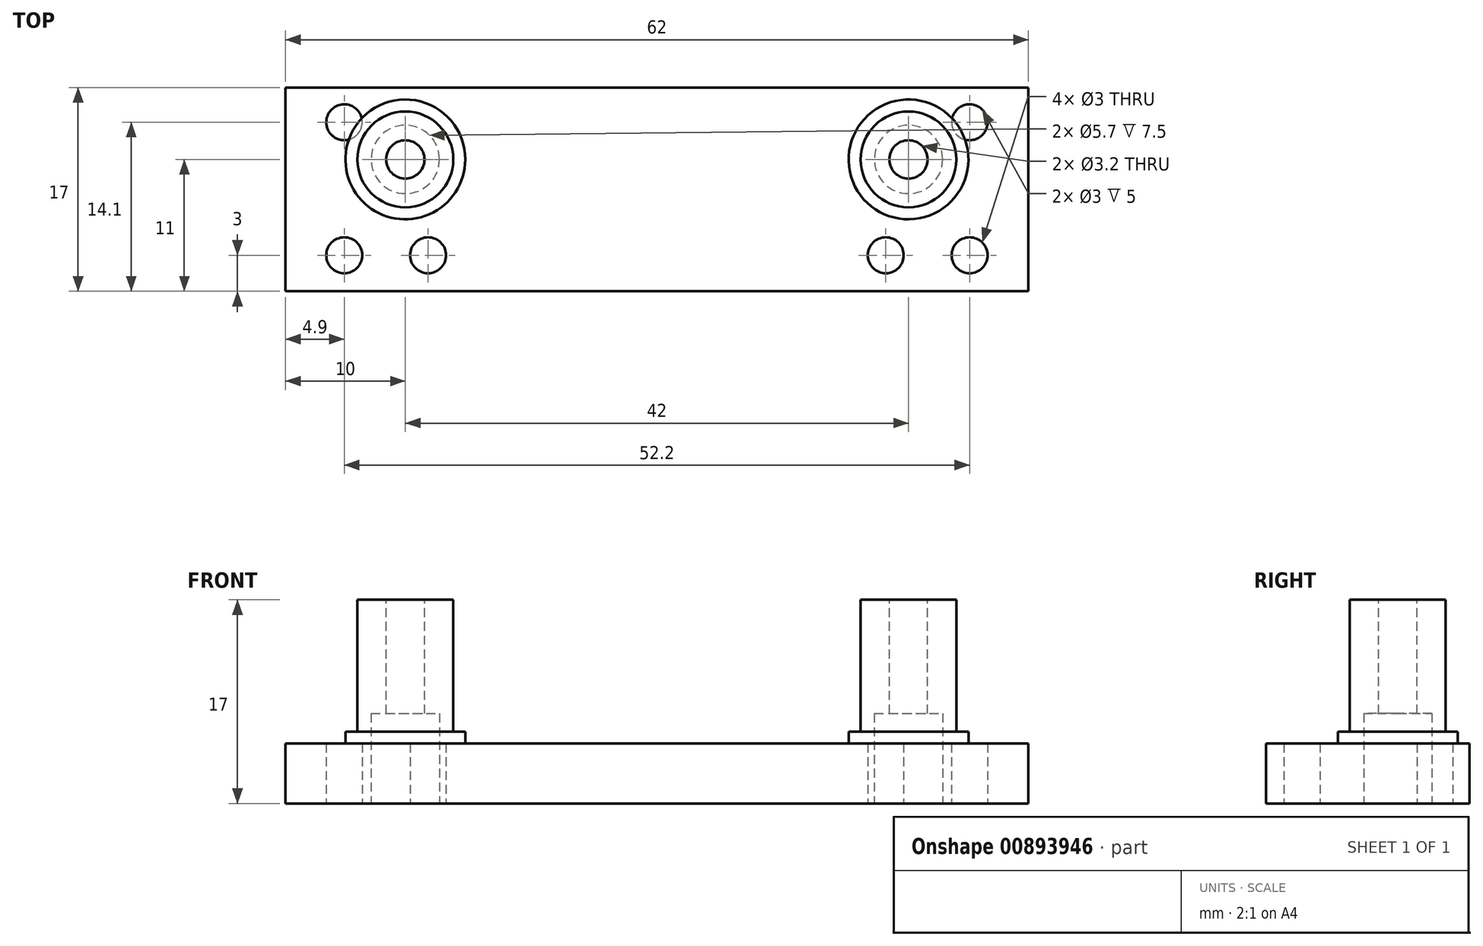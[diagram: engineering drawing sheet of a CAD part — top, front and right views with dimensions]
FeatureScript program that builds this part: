
annotation { "Feature Type Name" : "Feature", "Feature Type Description" : "" }
export const myFeature = defineFeature(function(context is Context, id is Id, definition is map)
    precondition{}
    {
        {
            var Q0;
            Q0=qCreatedBy(makeId("Top.planeOp"),FACE);
            var sketch = newSketch(context, id + "F0", { "sketchPlane" : qUnion([Q0])});
            skLineSegment(sketch, "E0.bottom", {"start": v(0, 0) * mm, "end": v(62, 0) * mm});
            skLineSegment(sketch, "E0.top", {"start": v(0, 17) * mm, "end": v(62, 17) * mm});
            skLineSegment(sketch, "E0.left", {"start": v(0, 0) * mm, "end": v(0, 17) * mm});
            skLineSegment(sketch, "E0.right", {"start": v(62, 0) * mm, "end": v(62, 17) * mm});
            skSolve(sketch);
        }
        {
            var Q0;
            Q0 = qSketchRegion(id + "F0", true);
            extrude(context, id + "F1", {"entities" : qUnion([Q0]), "depth" : 5 * mm, "offsetDistance" : 25 * mm});
        }
        {
            var Q0;
            Q0=makeQuery(id+"F1.opExtrude","CAP_FACE",FACE,{"disambiguationData":[OSD([sQuery(id+"F0.wireOp",EDGE,"E0.bottom"),sQuery(id+"F0.wireOp",EDGE,"E0.top"),sQuery(id+"F0.wireOp",EDGE,"E0.left"),sQuery(id+"F0.wireOp",EDGE,"E0.right")])],"isStart":false});
            var sketch = newSketch(context, id + "F2", { "sketchPlane" : qUnion([Q0])});
            skLineSegment(sketch, "E1", {"start": v(31, 17) * mm, "end": v(31, 0) * mm, "construction": true});
            skLineSegment(sketch, "E2", {"start": v(0, 11) * mm, "end": v(62, 11) * mm, "construction": true});
            skCircle(sketch, "E3", {"center": v(10, 11) * mm, "radius": 5 * mm});
            skCircle(sketch, "E4.MirrorC", {"center": v(52, 11) * mm, "radius": 5 * mm});
            skSolve(sketch);
        }
        {
            var Q0;
            Q0 = qSketchRegion(id + "F2", true);
            extrude(context, id + "F3", {"entities" : qUnion([Q0]), "operationType" : NewBodyOperationType.ADD, "depth" : 1 * mm, "offsetDistance" : 25 * mm});
        }
        {
            var Q0;
            Q0=makeQuery(id+"F3.opExtrude","CAP_FACE",FACE,{"disambiguationData":[OSD([sQuery(id+"F2.wireOp",EDGE,"E4.MirrorC")])],"isStart":false});
            var sketch = newSketch(context, id + "F4", { "sketchPlane" : qUnion([Q0])});
            skCircle(sketch, "E5", {"center": v(52, 11) * mm, "radius": 4 * mm});
            skCircle(sketch, "E6.MirrorC", {"center": v(10, 11) * mm, "radius": 4 * mm});
            skSolve(sketch);
        }
        {
            var Q0;
            Q0 = qSketchRegion(id + "F4", true);
            extrude(context, id + "F5", {"entities" : qUnion([Q0]), "operationType" : NewBodyOperationType.ADD, "depth" : 11 * mm, "offsetDistance" : 25 * mm});
        }
        {
            var Q0;
            Q0=makeQuery(id+"F1.opExtrude","CAP_FACE",FACE,{"disambiguationData":[OSD([sQuery(id+"F0.wireOp",EDGE,"E0.bottom"),sQuery(id+"F0.wireOp",EDGE,"E0.top"),sQuery(id+"F0.wireOp",EDGE,"E0.left"),sQuery(id+"F0.wireOp",EDGE,"E0.right")])],"isStart":true});
            var sketch = newSketch(context, id + "F6", { "sketchPlane" : qUnion([Q0])});
            skCircle(sketch, "E7", {"center": v(52, -11) * mm, "radius": 2.85 * mm});
            skCircle(sketch, "E8.MirrorC", {"center": v(10, -11) * mm, "radius": 2.85 * mm});
            skSolve(sketch);
        }
        {
            var Q0;
            Q0 = qSketchRegion(id + "F6", true);
            extrude(context, id + "F7", {"entities" : qUnion([Q0]), "operationType" : NewBodyOperationType.REMOVE, "oppositeDirection" : true, "depth" : 7.5 * mm, "offsetDistance" : 25 * mm});
        }
        {
            var Q0;
            Q0=makeQuery(id+"F5.opExtrude","CAP_FACE",FACE,{"disambiguationData":[OSD([sQuery(id+"F4.wireOp",EDGE,"E5")])],"isStart":false});
            var sketch = newSketch(context, id + "F8", { "sketchPlane" : qUnion([Q0])});
            skCircle(sketch, "E9", {"center": v(52, 11) * mm, "radius": 1.6 * mm});
            skCircle(sketch, "E10.MirrorC", {"center": v(10, 11) * mm, "radius": 1.6 * mm});
            skSolve(sketch);
        }
        {
            var Q0;
            Q0 = qSketchRegion(id + "F8", true);
            extrude(context, id + "F9", {"entities" : qUnion([Q0]), "operationType" : NewBodyOperationType.REMOVE, "oppositeDirection" : true, "depth" : 25 * mm, "offsetDistance" : 25 * mm});
        }
        {
            var Q0;
            Q0=makeQuery(id+"F1.opExtrude","CAP_FACE",FACE,{"disambiguationData":[OSD([sQuery(id+"F0.wireOp",EDGE,"E0.bottom"),sQuery(id+"F0.wireOp",EDGE,"E0.top"),sQuery(id+"F0.wireOp",EDGE,"E0.left"),sQuery(id+"F0.wireOp",EDGE,"E0.right")])],"isStart":true});
            var sketch = newSketch(context, id + "F10", { "sketchPlane" : qUnion([Q0])});
            skLineSegment(sketch, "E11", {"start": v(57.1, 0) * mm, "end": v(57.1, -17) * mm, "construction": true});
            skLineSegment(sketch, "E12", {"start": v(0, -3) * mm, "end": v(62, -3) * mm, "construction": true});
            skLineSegment(sketch, "E13", {"start": v(50.1, 0) * mm, "end": v(50.1, -17) * mm, "construction": true});
            skLineSegment(sketch, "E14", {"start": v(0, -14.1) * mm, "end": v(62, -14.1) * mm, "construction": true});
            skCircle(sketch, "E15", {"center": v(57.1, -14.1) * mm, "radius": 1.5 * mm});
            skCircle(sketch, "E16", {"center": v(50.1, -3) * mm, "radius": 1.5 * mm});
            skCircle(sketch, "E17.MirrorC", {"center": v(11.9, -3) * mm, "radius": 1.5 * mm});
            skCircle(sketch, "E18.MirrorC", {"center": v(4.9, -14.1) * mm, "radius": 1.5 * mm});
            skCircle(sketch, "E19", {"center": v(57.1, -3) * mm, "radius": 1.5 * mm});
            skCircle(sketch, "E20.MirrorC", {"center": v(4.9, -3) * mm, "radius": 1.5 * mm});
            skSolve(sketch);
        }
        {
            var Q0;
            Q0 = qSketchRegion(id + "F10", true);
            var Q1;
            Q1=makeQuery(id+"F1.opExtrude","CAP_FACE",FACE,{"disambiguationData":[OSD([sQuery(id+"F0.wireOp",EDGE,"E0.bottom"),sQuery(id+"F0.wireOp",EDGE,"E0.top"),sQuery(id+"F0.wireOp",EDGE,"E0.left"),sQuery(id+"F0.wireOp",EDGE,"E0.right")])],"isStart":false});
            extrude(context, id + "F11", {"entities" : qUnion([Q0]), "operationType" : NewBodyOperationType.REMOVE, "endBound" : BoundingType.UP_TO_SURFACE, "oppositeDirection" : true, "depth" : 25 * mm, "endBoundEntityFace" : qUnion([Q1]), "offsetDistance" : 25 * mm});
        }
    });
